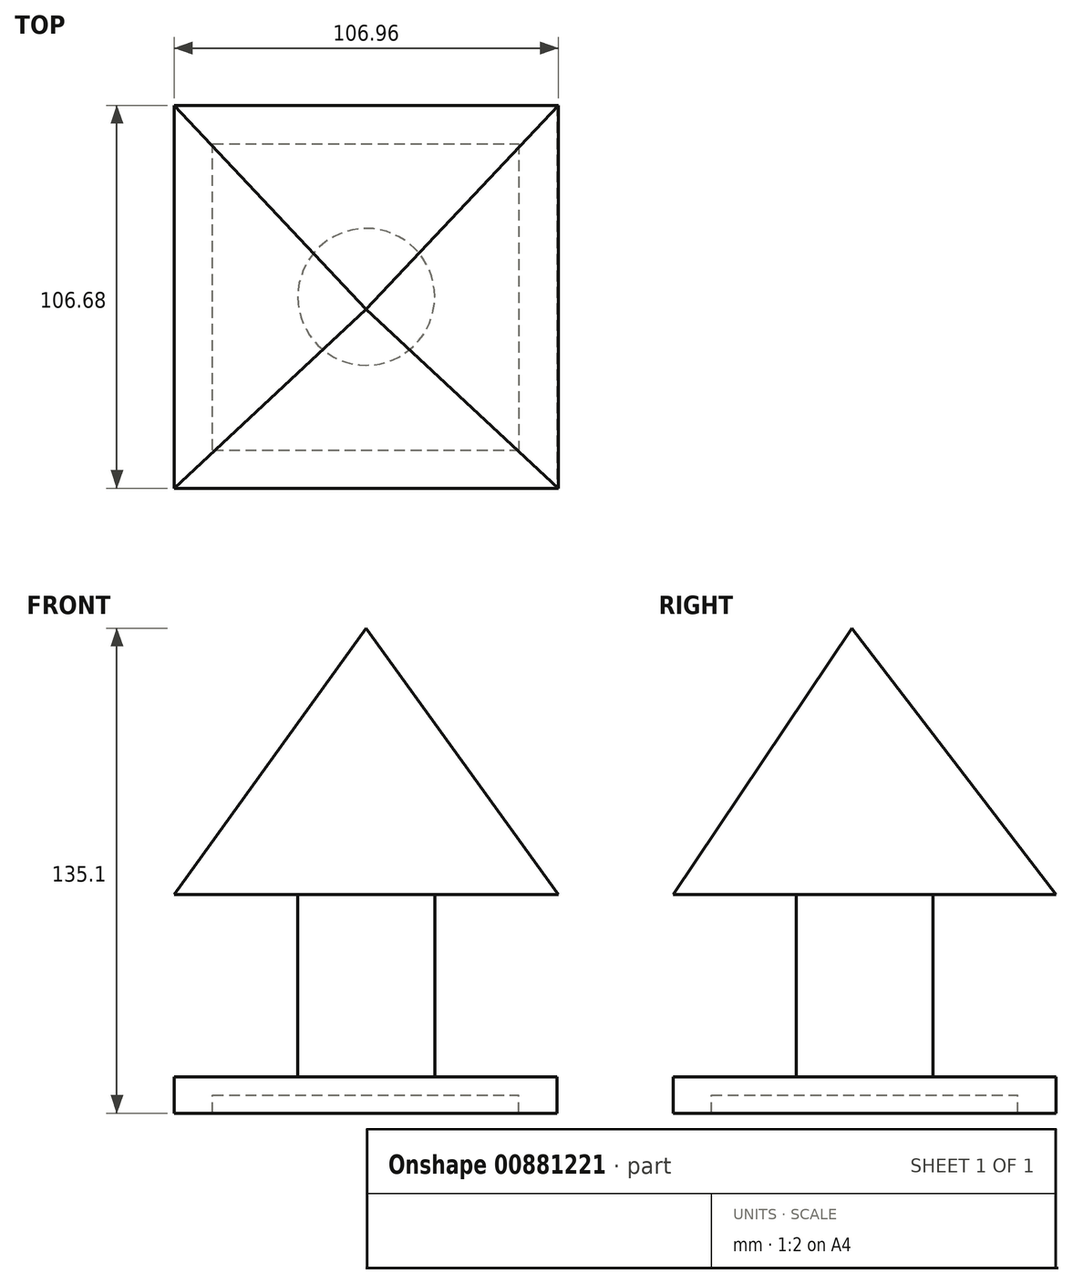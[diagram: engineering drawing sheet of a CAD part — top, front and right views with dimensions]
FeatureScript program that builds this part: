
annotation { "Feature Type Name" : "Feature", "Feature Type Description" : "" }
export const myFeature = defineFeature(function(context is Context, id is Id, definition is map)
    precondition{}
    {
        {
            var Q0;
            Q0=qCreatedBy(makeId("Top.planeOp"),FACE);
            var sketch = newSketch(context, id + "F0", { "sketchPlane" : qUnion([Q0])});
            skLineSegment(sketch, "E0.bottom", {"start": v(-53.48, 56.85) * mm, "end": v(53.2, 56.85) * mm});
            skLineSegment(sketch, "E0.top", {"start": v(-53.48, -49.83) * mm, "end": v(53.2, -49.83) * mm});
            skLineSegment(sketch, "E0.left", {"start": v(-53.48, 56.85) * mm, "end": v(-53.48, -49.83) * mm});
            skLineSegment(sketch, "E0.right", {"start": v(53.2, 56.85) * mm, "end": v(53.2, -49.83) * mm});
            skSolve(sketch);
        }
        {
            var Q0;
            Q0=makeQuery(id+"F0.imprint","IMPRINT",FACE,{"disambiguationData":[TD([[makeQuery(id+"F0.imprint","IMPRINT",EDGE,{"derivedFrom":sQuery(id+"F0.wireOp",EDGE,"E0.bottom")}),-1.0]])]});
            extrude(context, id + "F1", {"entities" : qUnion([Q0]), "depth" : 5.08 * mm, "offsetDistance" : 25.4 * mm});
        }
        {
            var Q0;
            Q0=makeQuery(id+"F1.opExtrude","CAP_FACE",FACE,{"disambiguationData":[OSD([sQuery(id+"F0.wireOp",EDGE,"E0.bottom"),sQuery(id+"F0.wireOp",EDGE,"E0.top"),sQuery(id+"F0.wireOp",EDGE,"E0.left"),sQuery(id+"F0.wireOp",EDGE,"E0.right")])],"isStart":true});
            var sketch = newSketch(context, id + "F2", { "sketchPlane" : qUnion([Q0])});
            skLineSegment(sketch, "E1.bottom", {"start": v(-53.48, 49.83) * mm, "end": v(53.2, 49.83) * mm});
            skLineSegment(sketch, "E1.top", {"start": v(-42.81, 39.16) * mm, "end": v(42.53, 39.16) * mm});
            skLineSegment(sketch, "E1.left", {"start": v(-53.48, 49.83) * mm, "end": v(-53.48, 39.16) * mm});
            skLineSegment(sketch, "E1.right", {"start": v(53.2, 49.83) * mm, "end": v(53.2, 39.16) * mm});
            skLineSegment(sketch, "E2.bottom", {"start": v(-53.48, 49.83) * mm, "end": v(-42.81, 49.83) * mm});
            skLineSegment(sketch, "E2.top", {"start": v(-53.48, -56.85) * mm, "end": v(-42.81, -56.85) * mm});
            skLineSegment(sketch, "E2.left", {"start": v(-53.48, 49.83) * mm, "end": v(-53.48, -56.85) * mm});
            skLineSegment(sketch, "E2.right", {"start": v(-42.81, 39.16) * mm, "end": v(-42.81, -46.18) * mm});
            skLineSegment(sketch, "E3.bottom", {"start": v(53.2, -56.85) * mm, "end": v(42.53, -56.85) * mm});
            skLineSegment(sketch, "E3.top", {"start": v(53.2, 49.83) * mm, "end": v(42.53, 49.83) * mm});
            skLineSegment(sketch, "E3.left", {"start": v(53.2, -56.85) * mm, "end": v(53.2, 49.83) * mm});
            skLineSegment(sketch, "E3.right", {"start": v(42.53, -46.18) * mm, "end": v(42.53, 39.16) * mm});
            skLineSegment(sketch, "E4.bottom", {"start": v(-53.48, -56.85) * mm, "end": v(53.2, -56.85) * mm});
            skLineSegment(sketch, "E4.top", {"start": v(-42.81, -46.18) * mm, "end": v(42.53, -46.18) * mm});
            skLineSegment(sketch, "E4.left", {"start": v(-53.48, -56.85) * mm, "end": v(-53.48, -46.18) * mm});
            skLineSegment(sketch, "E4.right", {"start": v(53.2, -56.85) * mm, "end": v(53.2, -46.18) * mm});
            skSolve(sketch);
        }
        {
            var Q0;
            Q0=makeQuery(id+"F2.imprint","IMPRINT",FACE,{"disambiguationData":[TD([[makeQuery(id+"F2.imprint","IMPRINT",EDGE,{"derivedFrom":sQuery(id+"F2.wireOp",EDGE,"E1.bottom")}),-1.0]])]});
            extrude(context, id + "F3", {"entities" : qUnion([Q0]), "operationType" : NewBodyOperationType.ADD, "depth" : 5.08 * mm, "offsetDistance" : 25.4 * mm});
        }
        {
            var Q0;
            Q0=makeQuery(id+"F1.opExtrude","CAP_FACE",FACE,{"disambiguationData":[OSD([sQuery(id+"F0.wireOp",EDGE,"E0.bottom"),sQuery(id+"F0.wireOp",EDGE,"E0.top"),sQuery(id+"F0.wireOp",EDGE,"E0.left"),sQuery(id+"F0.wireOp",EDGE,"E0.right")])],"isStart":false});
            var sketch = newSketch(context, id + "F4", { "sketchPlane" : qUnion([Q0])});
            skCircle(sketch, "E5", {"center": v(0, 3.5) * mm, "radius": 19.05 * mm});
            skPoint(sketch, "E6.orphan", {"position": v(-0.14, 56.85) * mm});
            skLineSegment(sketch, "E7.trimOffspring", {"start": v(-0.14, 3.5) * mm, "end": v(0, 3.5) * mm});
            skLineSegment(sketch, "E8.trimOffspring", {"start": v(0, 3.5) * mm, "end": v(-0.14, 3.5) * mm});
            skPoint(sketch, "E9.start.orphan", {"position": v(53.2, 3.5) * mm});
            skPoint(sketch, "E10.start.orphan", {"position": v(-53.48, 3.5) * mm});
            skPoint(sketch, "E11.end.orphan", {"position": v(-0.14, -49.83) * mm});
            skSolve(sketch);
        }
        {
            var Q0;
            Q0=makeQuery(id+"F4.imprint","IMPRINT",FACE,{"disambiguationData":[TD([[makeQuery(id+"F4.imprint","IMPRINT",EDGE,{"derivedFrom":sQuery(id+"F4.wireOp",EDGE,"E5")}),1.0]])]});
            extrude(context, id + "F5", {"entities" : qUnion([Q0]), "operationType" : NewBodyOperationType.ADD, "depth" : 50.8 * mm, "offsetDistance" : 25.4 * mm});
        }
        {
            var Q0;
            Q0=makeQuery(id+"F5.opExtrude","CAP_FACE",FACE,{"disambiguationData":[OSD([sQuery(id+"F4.wireOp",EDGE,"E5")])],"isStart":false});
            var sketch = newSketch(context, id + "F6", { "sketchPlane" : qUnion([Q0])});
            skLineSegment(sketch, "E12.bottom", {"start": v(-53.48, 56.85) * mm, "end": v(53.48, 56.85) * mm});
            skLineSegment(sketch, "E12.top", {"start": v(-53.48, -49.83) * mm, "end": v(53.48, -49.83) * mm});
            skLineSegment(sketch, "E12.left", {"start": v(-53.48, 56.85) * mm, "end": v(-53.48, -49.83) * mm});
            skLineSegment(sketch, "E12.right", {"start": v(53.48, 56.85) * mm, "end": v(53.48, -49.83) * mm});
            skPoint(sketch, "E12.middle", {"position": v(0, 3.5) * mm});
            skSolve(sketch);
        }
        {
            var Q0;
            Q0=qCreatedBy(makeId("Front.planeOp"),FACE);
            var sketch = newSketch(context, id + "F7", { "sketchPlane" : qUnion([Q0])});
            skPoint(sketch, "E13.start.orphan", {"position": v(0, 56.68) * mm});
            skLineSegment(sketch, "E14", {"start": v(0, 56.68) * mm, "end": v(0, 130.02) * mm});
            skLineSegment(sketch, "E15", {"start": v(0, 130.02) * mm, "end": v(0, 56.68) * mm});
            skSolve(sketch);
        }
        {
            var Q0;
            Q0 = qSketchRegion(id + "F6", true);
            var Q1;
            Q1=sQuery(id+"F7.wireOp",VERTEX,"E14.end");
            loft(context, id + "F8", {"sheetProfilesArray" : [{ "sheetProfileEntities" : qUnion([Q0]) }, { "sheetProfileEntities" : qUnion([Q1]) }]});
        }
    });
